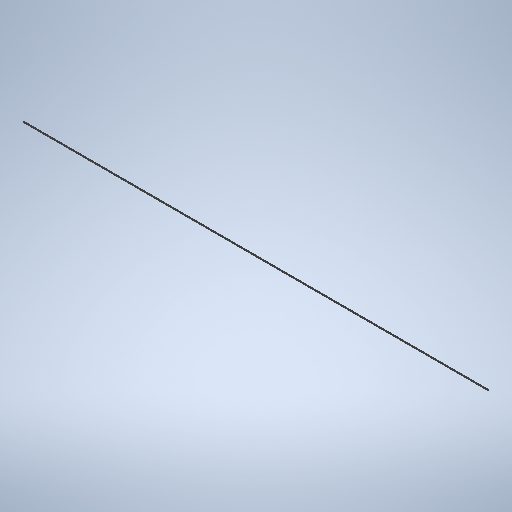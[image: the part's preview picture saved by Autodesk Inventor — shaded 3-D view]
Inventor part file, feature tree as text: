
AUTODESK INVENTOR PART (.ipt)
format: ipt  version: 2025.1 (Build 291241020, 241B)  size: 252,416 bytes
history: native  units: in
note: dims shown in document units (in); Inventor stores cm internally (conversion verified against a paired STEP export)
features: extrude x1, sketch x1
ambient origin geometry x8: Origin, YZ Plane, XZ Plane, XY Plane, X Axis, Y Axis, Z Axis, Center Point
bodies: Solid1 (feature_tree)
feature tree (2):
  extrude  "Extrusion1"  Depth=6.0in
  sketch  "Sketch1"  dims[d0=0.008in d1=6.0in d2=0.008in d3=0.0in]
